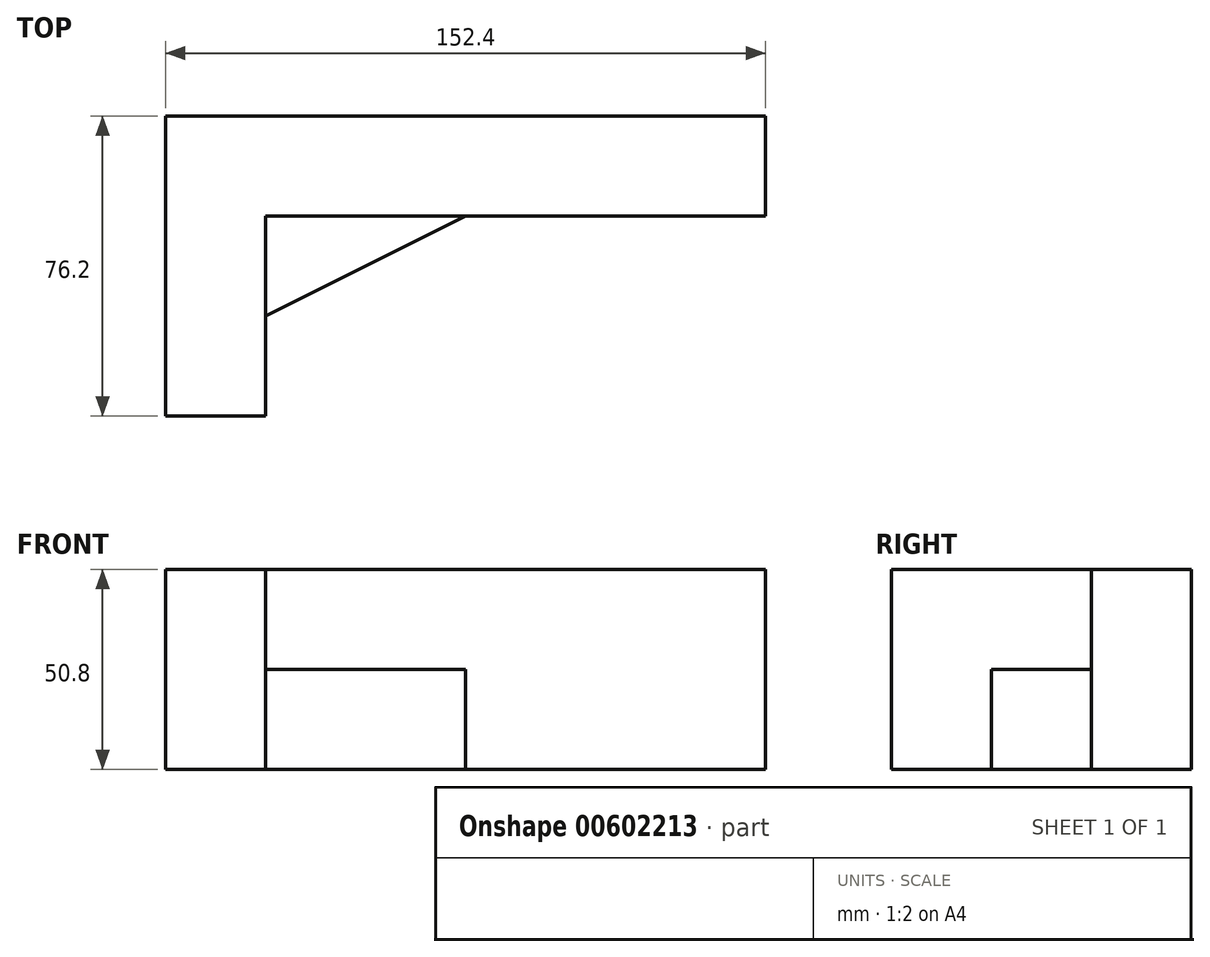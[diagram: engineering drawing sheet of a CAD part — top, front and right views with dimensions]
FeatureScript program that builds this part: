
annotation { "Feature Type Name" : "Feature", "Feature Type Description" : "" }
export const myFeature = defineFeature(function(context is Context, id is Id, definition is map)
    precondition{}
    {
        {
            var Q0;
            Q0=qCreatedBy(makeId("Front.planeOp"),FACE);
            var sketch = newSketch(context, id + "F0", { "sketchPlane" : qUnion([Q0])});
            skLineSegment(sketch, "E0", {"start": v(0, 0) * mm, "end": v(152.4, 0) * mm});
            skLineSegment(sketch, "E1", {"start": v(152.4, 0) * mm, "end": v(152.4, 50.8) * mm});
            skLineSegment(sketch, "E2", {"start": v(152.4, 50.8) * mm, "end": v(0, 50.8) * mm});
            skLineSegment(sketch, "E3", {"start": v(0, 50.8) * mm, "end": v(0, 0) * mm});
            skSolve(sketch);
        }
        {
            var Q0;
            Q0=makeQuery(id+"F0.imprint","IMPRINT",FACE,{"disambiguationData":[TD([[makeQuery(id+"F0.imprint","IMPRINT",EDGE,{"derivedFrom":sQuery(id+"F0.wireOp",EDGE,"E0")}),1.0]])]});
            extrude(context, id + "F1", {"entities" : qUnion([Q0]), "depth" : 25.4 * mm, "offsetDistance" : 25.4 * mm});
        }
        {
            var Q0;
            Q0=makeQuery(id+"F1.opExtrude","CAP_FACE",FACE,{"disambiguationData":[OSD([sQuery(id+"F0.wireOp",EDGE,"E0"),sQuery(id+"F0.wireOp",EDGE,"E1"),sQuery(id+"F0.wireOp",EDGE,"E2"),sQuery(id+"F0.wireOp",EDGE,"E3")])],"isStart":false});
            var sketch = newSketch(context, id + "F2", { "sketchPlane" : qUnion([Q0])});
            skLineSegment(sketch, "E4", {"start": v(25.4, 50.8) * mm, "end": v(25.4, 0) * mm});
            skLineSegment(sketch, "E5", {"start": v(25.4, 0) * mm, "end": v(0, 0) * mm});
            skLineSegment(sketch, "E6", {"start": v(0, 0) * mm, "end": v(0, 50.8) * mm});
            skLineSegment(sketch, "E7", {"start": v(0, 50.8) * mm, "end": v(25.4, 50.8) * mm});
            skSolve(sketch);
        }
        {
            var Q0;
            Q0 = qSketchRegion(id + "F2", true);
            extrude(context, id + "F3", {"entities" : qUnion([Q0]), "operationType" : NewBodyOperationType.ADD, "depth" : 50.8 * mm, "offsetDistance" : 25.4 * mm});
        }
        {
            var Q0;
            Q0=makeQuery(id+"F3.opExtrude","SWEPT_FACE",FACE,{"disambiguationData":[OSD([sQuery(id+"F2.wireOp",EDGE,"E4")])]});
            var sketch = newSketch(context, id + "F4", { "sketchPlane" : qUnion([Q0])});
            skLineSegment(sketch, "E8.bottom", {"start": v(-25.4, 0) * mm, "end": v(-50.8, 0) * mm});
            skLineSegment(sketch, "E8.top", {"start": v(-25.4, 25.4) * mm, "end": v(-50.8, 25.4) * mm});
            skLineSegment(sketch, "E8.left", {"start": v(-25.4, 0) * mm, "end": v(-25.4, 25.4) * mm});
            skLineSegment(sketch, "E8.right", {"start": v(-50.8, 0) * mm, "end": v(-50.8, 25.4) * mm});
            skSolve(sketch);
        }
        {
            var Q0;
            Q0 = qSketchRegion(id + "F4", true);
            extrude(context, id + "F5", {"entities" : qUnion([Q0]), "operationType" : NewBodyOperationType.ADD, "depth" : 50.8 * mm, "offsetDistance" : 25.4 * mm});
        }
        {
            var Q0;
            Q0=makeQuery(id+"F5.opExtrude","SWEPT_FACE",FACE,{"disambiguationData":[OSD([sQuery(id+"F4.wireOp",EDGE,"E8.top")])]});
            var sketch = newSketch(context, id + "F6", { "sketchPlane" : qUnion([Q0])});
            skLineSegment(sketch, "E9", {"start": v(76.2, -25.4) * mm, "end": v(25.4, -50.8) * mm});
            skSolve(sketch);
        }
        {
            var Q0;
            Q0=makeQuery(id+"F6.imprint","IMPRINT",FACE,{"disambiguationData":[TD([[makeQuery(id+"F6.imprint","IMPRINT",EDGE,{"derivedFrom":sQuery(id+"F6.wireOp",EDGE,"E9")}),1.0]])]});
            extrude(context, id + "F7", {"entities" : qUnion([Q0]), "operationType" : NewBodyOperationType.REMOVE, "oppositeDirection" : true, "depth" : 2540 * mm, "offsetDistance" : 25.4 * mm});
        }
    });
